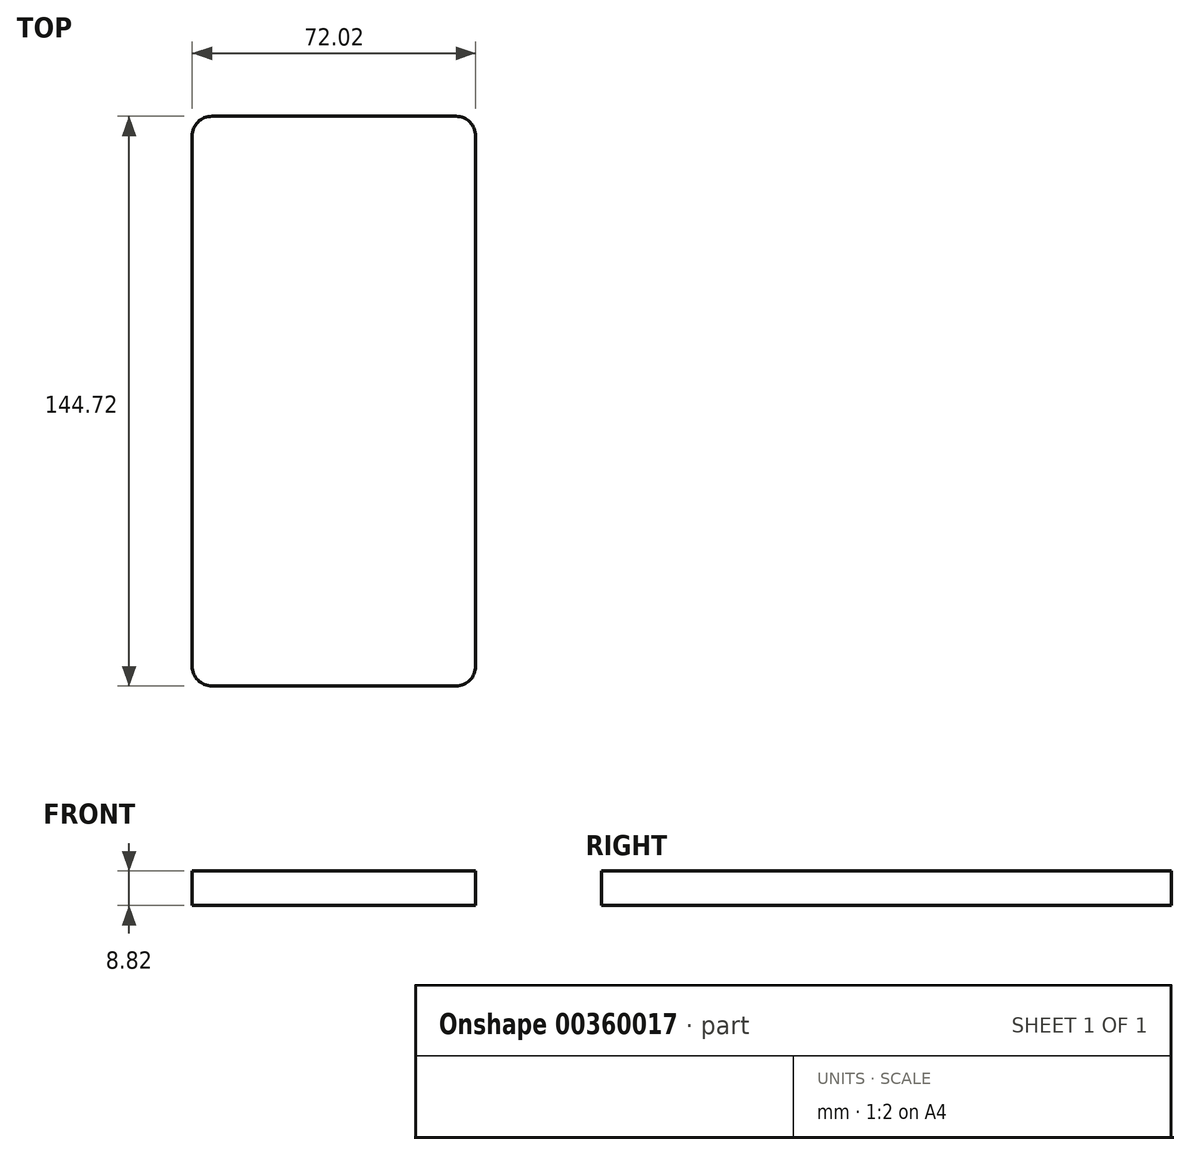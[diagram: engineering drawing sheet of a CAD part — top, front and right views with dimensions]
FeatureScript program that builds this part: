
annotation { "Feature Type Name" : "Feature", "Feature Type Description" : "" }
export const myFeature = defineFeature(function(context is Context, id is Id, definition is map)
    precondition{}
    {
        {
            var Q0;
            Q0=qCreatedBy(makeId("Top.planeOp"),FACE);
            var sketch = newSketch(context, id + "F0", { "sketchPlane" : qUnion([Q0])});
            skLineSegment(sketch, "E0.bottom", {"start": v(-32.05, 73.33) * mm, "end": v(29.97, 73.33) * mm});
            skLineSegment(sketch, "E0.top", {"start": v(-32.05, -71.4) * mm, "end": v(29.97, -71.4) * mm});
            skLineSegment(sketch, "E0.left", {"start": v(-37.05, 68.33) * mm, "end": v(-37.05, -66.4) * mm});
            skLineSegment(sketch, "E0.right", {"start": v(34.97, 68.33) * mm, "end": v(34.97, -66.4) * mm});
            skPoint(sketch, "E1.visualSharp", {"position": v(-37.05, 73.33) * mm});
            skArc(sketch, "E1.filletArc", {"start": v(-32.05, 73.33) * mm, "mid": v(-35.59, 71.86) * mm, "end": v(-37.05, 68.33) * mm});
            skPoint(sketch, "E2.visualSharp", {"position": v(34.97, 73.33) * mm});
            skArc(sketch, "E2.filletArc", {"start": v(34.97, 68.33) * mm, "mid": v(33.5, 71.86) * mm, "end": v(29.97, 73.33) * mm});
            skPoint(sketch, "E3.visualSharp", {"position": v(34.97, -71.4) * mm});
            skArc(sketch, "E3.filletArc", {"start": v(29.97, -71.4) * mm, "mid": v(33.5, -69.93) * mm, "end": v(34.97, -66.4) * mm});
            skPoint(sketch, "E4.visualSharp", {"position": v(-37.05, -71.4) * mm});
            skArc(sketch, "E4.filletArc", {"start": v(-37.05, -66.4) * mm, "mid": v(-35.59, -69.93) * mm, "end": v(-32.05, -71.4) * mm});
            skSolve(sketch);
        }
        {
            var Q0;
            Q0 = qSketchRegion(id + "F0", true);
            extrude(context, id + "F1", {"entities" : qUnion([Q0]), "depth" : 8.82 * mm});
        }
    });
